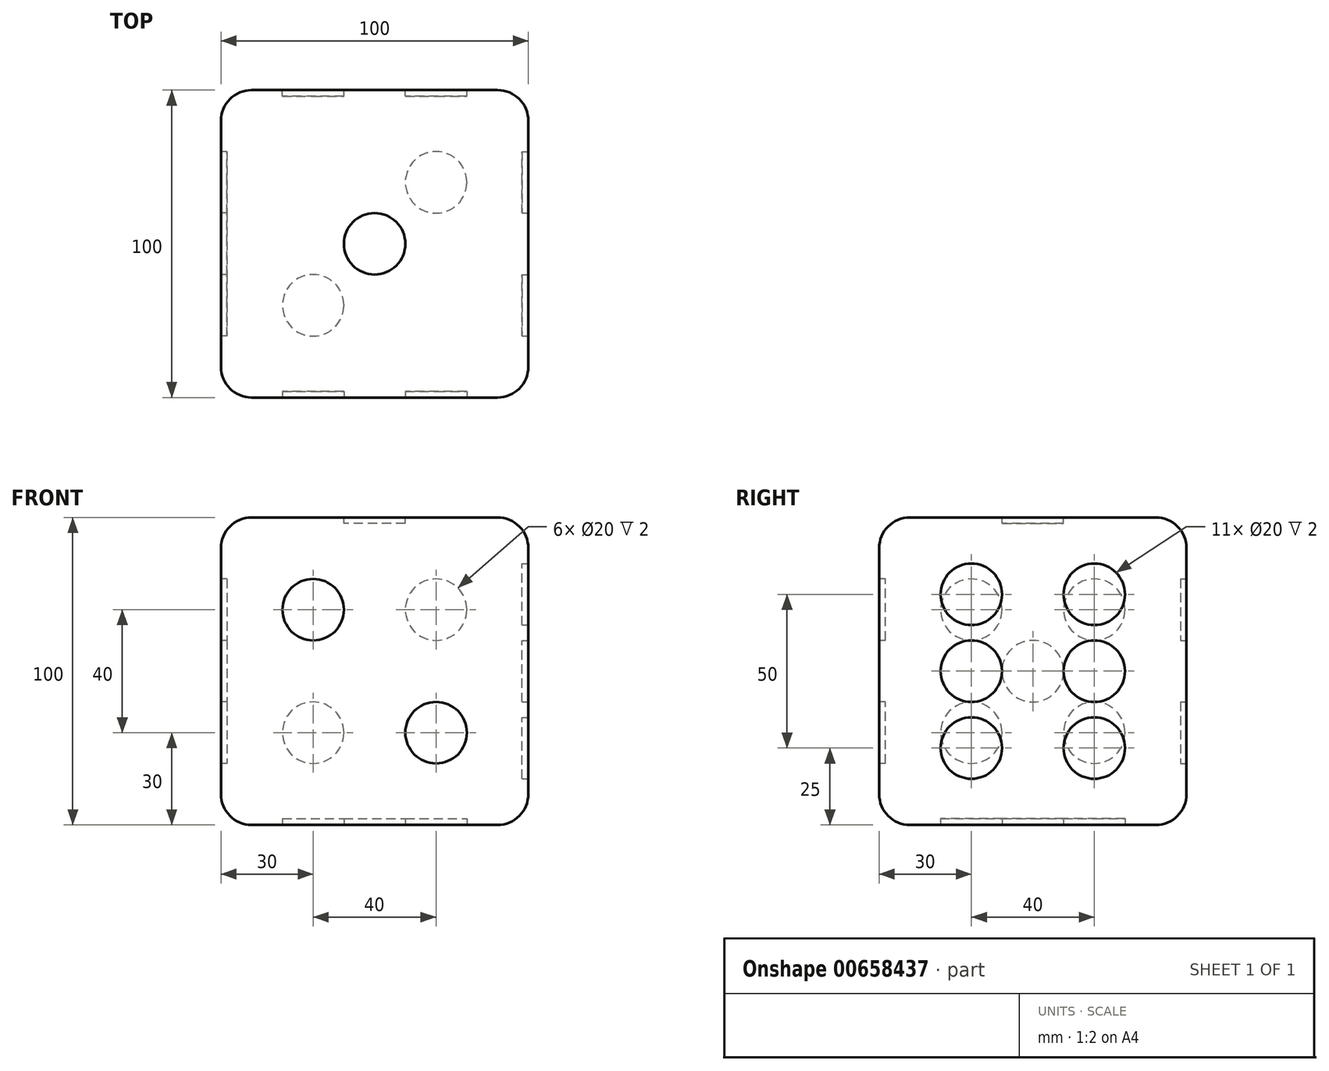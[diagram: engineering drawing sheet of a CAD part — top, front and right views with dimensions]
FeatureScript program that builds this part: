
annotation { "Feature Type Name" : "Feature", "Feature Type Description" : "" }
export const myFeature = defineFeature(function(context is Context, id is Id, definition is map)
    precondition{}
    {
        {
            var Q0;
            Q0=qCreatedBy(makeId("Top.planeOp"),FACE);
            var sketch = newSketch(context, id + "F0", { "sketchPlane" : qUnion([Q0])});
            skLineSegment(sketch, "E0.bottom", {"start": v(50, -50) * mm, "end": v(-50, -50) * mm});
            skLineSegment(sketch, "E0.top", {"start": v(50, 50) * mm, "end": v(-50, 50) * mm});
            skLineSegment(sketch, "E0.left", {"start": v(50, -50) * mm, "end": v(50, 50) * mm});
            skLineSegment(sketch, "E0.right", {"start": v(-50, -50) * mm, "end": v(-50, 50) * mm});
            skPoint(sketch, "E0.middle", {"position": v(0, 0) * mm});
            skSolve(sketch);
        }
        {
            var Q0;
            Q0 = qSketchRegion(id + "F0", true);
            extrude(context, id + "F1", {"entities" : qUnion([Q0]), "endBound" : BoundingType.SYMMETRIC, "depth" : 100 * mm, "offsetDistance" : 25 * mm});
        }
        {
            var Q0;
            Q0=makeQuery(id+"F1.opExtrude","SWEPT_EDGE",EDGE,{"disambiguationData":[OSD([sQuery(id+"F0.wireOp",EDGE,"E0.top"),sQuery(id+"F0.wireOp",EDGE,"E0.left")])]});
            var Q1;
            Q1=makeQuery(id+"F1.opExtrude","SWEPT_EDGE",EDGE,{"disambiguationData":[OSD([sQuery(id+"F0.wireOp",EDGE,"E0.bottom"),sQuery(id+"F0.wireOp",EDGE,"E0.right")])]});
            var Q2;
            Q2=makeQuery(id+"F1.opExtrude","SWEPT_EDGE",EDGE,{"disambiguationData":[OSD([sQuery(id+"F0.wireOp",EDGE,"E0.bottom"),sQuery(id+"F0.wireOp",EDGE,"E0.left")])]});
            var Q3;
            Q3=makeQuery(id+"F1.opExtrude","CAP_EDGE",EDGE,{"disambiguationData":[OSD([sQuery(id+"F0.wireOp",EDGE,"E0.bottom")])],"isStart":true});
            var Q4;
            Q4=makeQuery(id+"F1.opExtrude","CAP_EDGE",EDGE,{"disambiguationData":[OSD([sQuery(id+"F0.wireOp",EDGE,"E0.bottom")])],"isStart":false});
            var Q5;
            Q5=makeQuery(id+"F1.opExtrude","CAP_EDGE",EDGE,{"disambiguationData":[OSD([sQuery(id+"F0.wireOp",EDGE,"E0.left")])],"isStart":true});
            var Q6;
            Q6=makeQuery(id+"F1.opExtrude","CAP_EDGE",EDGE,{"disambiguationData":[OSD([sQuery(id+"F0.wireOp",EDGE,"E0.left")])],"isStart":false});
            var Q7;
            Q7=makeQuery(id+"F1.opExtrude","CAP_EDGE",EDGE,{"disambiguationData":[OSD([sQuery(id+"F0.wireOp",EDGE,"E0.right")])],"isStart":false});
            var Q8;
            Q8=makeQuery(id+"F1.opExtrude","SWEPT_EDGE",EDGE,{"disambiguationData":[OSD([sQuery(id+"F0.wireOp",EDGE,"E0.top"),sQuery(id+"F0.wireOp",EDGE,"E0.right")])]});
            var Q9;
            Q9=makeQuery(id+"F1.opExtrude","CAP_EDGE",EDGE,{"disambiguationData":[OSD([sQuery(id+"F0.wireOp",EDGE,"E0.top")])],"isStart":true});
            var Q10;
            Q10=makeQuery(id+"F1.opExtrude","CAP_EDGE",EDGE,{"disambiguationData":[OSD([sQuery(id+"F0.wireOp",EDGE,"E0.top")])],"isStart":false});
            var Q11;
            Q11=makeQuery(id+"F1.opExtrude","CAP_EDGE",EDGE,{"disambiguationData":[OSD([sQuery(id+"F0.wireOp",EDGE,"E0.right")])],"isStart":true});
            fillet(context, id + "F2", {"entities" : qUnion([Q0, Q1, Q2, Q3, Q4, Q5, Q6, Q7, Q8, Q9, Q10, Q11]), "radius" : 10 * mm, "tangentPropagation" : true, "allowEdgeOverflow" : false});
        }
        {
            var Q0;
            Q0=makeQuery(id+"F1.opExtrude","CAP_FACE",FACE,{"disambiguationData":[OSD([sQuery(id+"F0.wireOp",EDGE,"E0.bottom"),sQuery(id+"F0.wireOp",EDGE,"E0.top"),sQuery(id+"F0.wireOp",EDGE,"E0.left"),sQuery(id+"F0.wireOp",EDGE,"E0.right")])],"isStart":false});
            var sketch = newSketch(context, id + "F3", { "sketchPlane" : qUnion([Q0])});
            skCircle(sketch, "E1", {"center": v(0, 0) * mm, "radius": 10 * mm});
            skSolve(sketch);
        }
        {
            var Q0;
            Q0 = qSketchRegion(id + "F3", true);
            extrude(context, id + "F4", {"entities" : qUnion([Q0]), "operationType" : NewBodyOperationType.REMOVE, "oppositeDirection" : true, "depth" : 2 * mm, "offsetDistance" : 25 * mm});
        }
        {
            var Q0;
            Q0=makeQuery(id+"F1.opExtrude","SWEPT_FACE",FACE,{"disambiguationData":[OSD([sQuery(id+"F0.wireOp",EDGE,"E0.bottom")])]});
            var sketch = newSketch(context, id + "F5", { "sketchPlane" : qUnion([Q0])});
            skCircle(sketch, "E2", {"center": v(-20, 20) * mm, "radius": 10 * mm});
            skCircle(sketch, "E3", {"center": v(20, -20) * mm, "radius": 10 * mm});
            skSolve(sketch);
        }
        {
            var Q0;
            Q0 = qSketchRegion(id + "F5", true);
            extrude(context, id + "F6", {"entities" : qUnion([Q0]), "operationType" : NewBodyOperationType.REMOVE, "oppositeDirection" : true, "depth" : 2 * mm, "offsetDistance" : 25 * mm});
        }
        {
            var Q0;
            Q0=makeQuery(id+"F1.opExtrude","CAP_FACE",FACE,{"disambiguationData":[OSD([sQuery(id+"F0.wireOp",EDGE,"E0.bottom"),sQuery(id+"F0.wireOp",EDGE,"E0.top"),sQuery(id+"F0.wireOp",EDGE,"E0.left"),sQuery(id+"F0.wireOp",EDGE,"E0.right")])],"isStart":true});
            var sketch = newSketch(context, id + "F7", { "sketchPlane" : qUnion([Q0])});
            skCircle(sketch, "E4", {"center": v(-20, 20) * mm, "radius": 10 * mm});
            skCircle(sketch, "E5", {"center": v(0, 0) * mm, "radius": 10 * mm});
            skCircle(sketch, "E6", {"center": v(20, -20) * mm, "radius": 10 * mm});
            skSolve(sketch);
        }
        {
            var Q0;
            Q0 = qSketchRegion(id + "F7", true);
            extrude(context, id + "F8", {"entities" : qUnion([Q0]), "operationType" : NewBodyOperationType.REMOVE, "oppositeDirection" : true, "depth" : 2 * mm, "offsetDistance" : 25 * mm});
        }
        {
            var Q0;
            Q0=makeQuery(id+"F1.opExtrude","SWEPT_FACE",FACE,{"disambiguationData":[OSD([sQuery(id+"F0.wireOp",EDGE,"E0.top")])]});
            var sketch = newSketch(context, id + "F9", { "sketchPlane" : qUnion([Q0])});
            skCircle(sketch, "E7", {"center": v(-20, 20) * mm, "radius": 10 * mm});
            skCircle(sketch, "E8", {"center": v(20, 20) * mm, "radius": 10 * mm});
            skCircle(sketch, "E9", {"center": v(20, -20) * mm, "radius": 10 * mm});
            skCircle(sketch, "E10", {"center": v(-20, -20) * mm, "radius": 10 * mm});
            skSolve(sketch);
        }
        {
            var Q0;
            Q0 = qSketchRegion(id + "F9", true);
            extrude(context, id + "F10", {"entities" : qUnion([Q0]), "operationType" : NewBodyOperationType.REMOVE, "oppositeDirection" : true, "depth" : 2 * mm, "offsetDistance" : 25 * mm});
        }
        {
            var Q0;
            Q0=makeQuery(id+"F1.opExtrude","SWEPT_FACE",FACE,{"disambiguationData":[OSD([sQuery(id+"F0.wireOp",EDGE,"E0.right")])]});
            var sketch = newSketch(context, id + "F11", { "sketchPlane" : qUnion([Q0])});
            skCircle(sketch, "E11", {"center": v(0, 0) * mm, "radius": 10 * mm});
            skCircle(sketch, "E12", {"center": v(-20, 20) * mm, "radius": 10 * mm});
            skCircle(sketch, "E13", {"center": v(20, 20) * mm, "radius": 10 * mm});
            skCircle(sketch, "E14", {"center": v(20, -20) * mm, "radius": 10 * mm});
            skCircle(sketch, "E15", {"center": v(-20, -20) * mm, "radius": 10 * mm});
            skSolve(sketch);
        }
        {
            var Q0;
            Q0 = qSketchRegion(id + "F11", true);
            extrude(context, id + "F12", {"entities" : qUnion([Q0]), "operationType" : NewBodyOperationType.REMOVE, "oppositeDirection" : true, "depth" : 2 * mm, "offsetDistance" : 25 * mm});
        }
        {
            var Q0;
            Q0=makeQuery(id+"F1.opExtrude","SWEPT_FACE",FACE,{"disambiguationData":[OSD([sQuery(id+"F0.wireOp",EDGE,"E0.left")])]});
            var sketch = newSketch(context, id + "F13", { "sketchPlane" : qUnion([Q0])});
            skCircle(sketch, "E16", {"center": v(-20, 25) * mm, "radius": 10 * mm});
            skCircle(sketch, "E17", {"center": v(-20, 0) * mm, "radius": 10 * mm});
            skCircle(sketch, "E18", {"center": v(-20, -25) * mm, "radius": 10 * mm});
            skCircle(sketch, "E19", {"center": v(20, -25) * mm, "radius": 10 * mm});
            skCircle(sketch, "E20", {"center": v(20, 0) * mm, "radius": 10 * mm});
            skCircle(sketch, "E21", {"center": v(20, 25) * mm, "radius": 10 * mm});
            skSolve(sketch);
        }
        {
            var Q0;
            Q0 = qSketchRegion(id + "F13", true);
            extrude(context, id + "F14", {"entities" : qUnion([Q0]), "operationType" : NewBodyOperationType.REMOVE, "oppositeDirection" : true, "depth" : 2 * mm, "offsetDistance" : 25 * mm});
        }
    });
